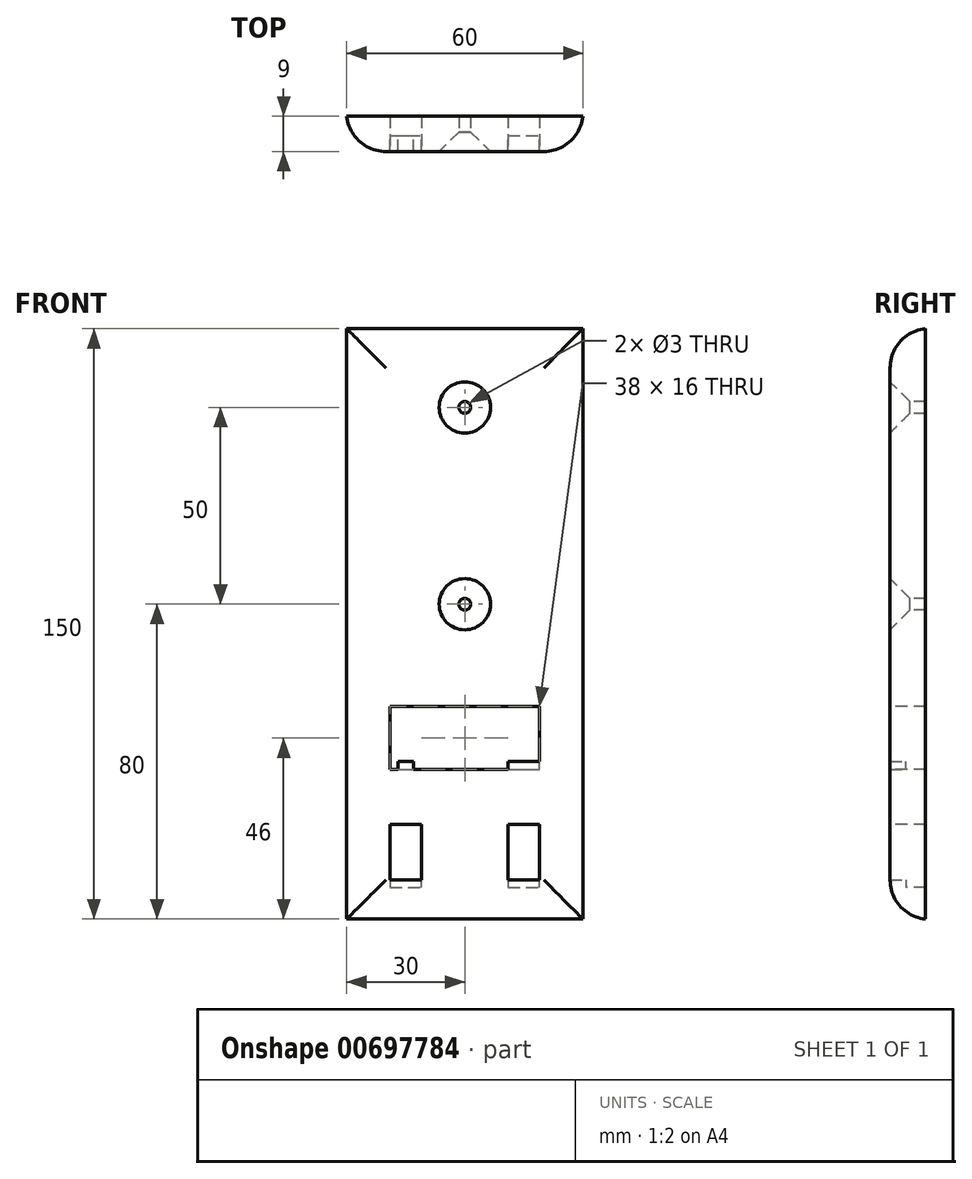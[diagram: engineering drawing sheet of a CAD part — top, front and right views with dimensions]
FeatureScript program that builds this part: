
annotation { "Feature Type Name" : "Feature", "Feature Type Description" : "" }
export const myFeature = defineFeature(function(context is Context, id is Id, definition is map)
    precondition{}
    {
        {
            var Q0;
            Q0=qCreatedBy(makeId("Front.planeOp"),FACE);
            var sketch = newSketch(context, id + "F0", { "sketchPlane" : qUnion([Q0])});
            skLineSegment(sketch, "E0", {"start": v(0, 0) * mm, "end": v(-30, 0) * mm});
            skLineSegment(sketch, "E1", {"start": v(-30, 0) * mm, "end": v(30, 0) * mm});
            skLineSegment(sketch, "E2", {"start": v(30, 0) * mm, "end": v(30, 80) * mm});
            skLineSegment(sketch, "E3", {"start": v(30, 80) * mm, "end": v(-30, 80) * mm});
            skLineSegment(sketch, "E4", {"start": v(-30, 80) * mm, "end": v(-30, 0) * mm});
            skLineSegment(sketch, "E5", {"start": v(-30, 0) * mm, "end": v(-30, 50) * mm, "construction": true});
            skLineSegment(sketch, "E6", {"start": v(-30, 50) * mm, "end": v(30, 50) * mm, "construction": true});
            skLineSegment(sketch, "E7", {"start": v(30, 50) * mm, "end": v(0, 50) * mm, "construction": true});
            skLineSegment(sketch, "E8", {"start": v(0, 50) * mm, "end": v(0, 20) * mm, "construction": true});
            skLineSegment(sketch, "E9", {"start": v(0, 20) * mm, "end": v(30, 20) * mm, "construction": true});
            skLineSegment(sketch, "E10", {"start": v(30, 20) * mm, "end": v(-30, 20) * mm, "construction": true});
            skPoint(sketch, "E10.endSnap0", {"position": v(15, 20) * mm});
            skLineSegment(sketch, "E11.bottom", {"start": v(15, 50) * mm, "end": v(-15, 50) * mm, "construction": true});
            skLineSegment(sketch, "E11.top", {"start": v(15, 20) * mm, "end": v(-15, 20) * mm, "construction": true});
            skLineSegment(sketch, "E11.left", {"start": v(15, 50) * mm, "end": v(15, 20) * mm, "construction": true});
            skLineSegment(sketch, "E11.right", {"start": v(-15, 50) * mm, "end": v(-15, 20) * mm, "construction": true});
            skPoint(sketch, "E11.middle", {"position": v(0, 35) * mm});
            skLineSegment(sketch, "E12", {"start": v(-15, 50) * mm, "end": v(15, 20) * mm, "construction": true});
            skLineSegment(sketch, "E13", {"start": v(15, 50) * mm, "end": v(-15, 20) * mm, "construction": true});
            skLineSegment(sketch, "E14.bottom", {"start": v(-11, 46) * mm, "end": v(-19, 46) * mm});
            skLineSegment(sketch, "E14.top", {"start": v(-11, 54) * mm, "end": v(-19, 54) * mm});
            skLineSegment(sketch, "E14.left", {"start": v(-11, 46) * mm, "end": v(-11, 54) * mm});
            skLineSegment(sketch, "E14.right", {"start": v(-19, 46) * mm, "end": v(-19, 54) * mm});
            skPoint(sketch, "E14.middle", {"position": v(-15, 50) * mm});
            skLineSegment(sketch, "E15.bottom", {"start": v(19, 46) * mm, "end": v(11, 46) * mm});
            skLineSegment(sketch, "E15.top", {"start": v(19, 54) * mm, "end": v(11, 54) * mm});
            skLineSegment(sketch, "E15.left", {"start": v(19, 46) * mm, "end": v(19, 54) * mm});
            skLineSegment(sketch, "E15.right", {"start": v(11, 46) * mm, "end": v(11, 54) * mm});
            skPoint(sketch, "E15.middle", {"position": v(15, 50) * mm});
            skLineSegment(sketch, "E16.bottom", {"start": v(-11, 16) * mm, "end": v(-19, 16) * mm});
            skLineSegment(sketch, "E16.top", {"start": v(-11, 24) * mm, "end": v(-19, 24) * mm});
            skLineSegment(sketch, "E16.left", {"start": v(-11, 16) * mm, "end": v(-11, 24) * mm});
            skLineSegment(sketch, "E16.right", {"start": v(-19, 16) * mm, "end": v(-19, 24) * mm});
            skPoint(sketch, "E16.middle", {"position": v(-15, 20) * mm});
            skLineSegment(sketch, "E17.bottom", {"start": v(19, 16) * mm, "end": v(11, 16) * mm});
            skLineSegment(sketch, "E17.top", {"start": v(19, 24) * mm, "end": v(11, 24) * mm});
            skLineSegment(sketch, "E17.left", {"start": v(19, 16) * mm, "end": v(19, 24) * mm});
            skLineSegment(sketch, "E17.right", {"start": v(11, 16) * mm, "end": v(11, 24) * mm});
            skLineSegment(sketch, "E18.bottom", {"start": v(-19, 46) * mm, "end": v(-11, 46) * mm});
            skLineSegment(sketch, "E18.left", {"start": v(-19, 46) * mm, "end": v(-19, 48) * mm});
            skLineSegment(sketch, "E18.right", {"start": v(-11, 46) * mm, "end": v(-11, 48) * mm});
            skLineSegment(sketch, "E19.top", {"start": v(-19, 38) * mm, "end": v(-11, 38) * mm});
            skLineSegment(sketch, "E19.left", {"start": v(-19, 46) * mm, "end": v(-19, 38) * mm});
            skLineSegment(sketch, "E19.right", {"start": v(-11, 46) * mm, "end": v(-11, 38) * mm});
            skLineSegment(sketch, "E20.bottom", {"start": v(11, 46) * mm, "end": v(19, 46) * mm});
            skLineSegment(sketch, "E20.top", {"start": v(11, 38) * mm, "end": v(19, 38) * mm});
            skLineSegment(sketch, "E20.left", {"start": v(11, 46) * mm, "end": v(11, 38) * mm});
            skLineSegment(sketch, "E20.right", {"start": v(19, 46) * mm, "end": v(19, 38) * mm});
            skLineSegment(sketch, "E21.bottom", {"start": v(-19, 16) * mm, "end": v(-11, 16) * mm});
            skLineSegment(sketch, "E21.top", {"start": v(-19, 8) * mm, "end": v(-11, 8) * mm});
            skLineSegment(sketch, "E21.left", {"start": v(-19, 16) * mm, "end": v(-19, 8) * mm});
            skLineSegment(sketch, "E21.right", {"start": v(-11, 16) * mm, "end": v(-11, 8) * mm});
            skLineSegment(sketch, "E22.bottom", {"start": v(11, 16) * mm, "end": v(19, 16) * mm});
            skLineSegment(sketch, "E22.top", {"start": v(11, 8) * mm, "end": v(19, 8) * mm});
            skLineSegment(sketch, "E22.left", {"start": v(11, 16) * mm, "end": v(11, 8) * mm});
            skLineSegment(sketch, "E22.right", {"start": v(19, 16) * mm, "end": v(19, 8) * mm});
            skLineSegment(sketch, "E23.bottom", {"start": v(-19, 46) * mm, "end": v(-17, 46) * mm});
            skLineSegment(sketch, "E23.top", {"start": v(-19, 38) * mm, "end": v(-17, 38) * mm});
            skLineSegment(sketch, "E23.right", {"start": v(-17, 46) * mm, "end": v(-17, 38) * mm});
            skLineSegment(sketch, "E24.bottom", {"start": v(-11, 46) * mm, "end": v(-13, 46) * mm});
            skLineSegment(sketch, "E24.top", {"start": v(-11, 38) * mm, "end": v(-13, 38) * mm});
            skLineSegment(sketch, "E24.right", {"start": v(-13, 46) * mm, "end": v(-13, 38) * mm});
            skLineSegment(sketch, "E25.bottom", {"start": v(11, 46) * mm, "end": v(13, 46) * mm});
            skLineSegment(sketch, "E25.top", {"start": v(11, 38) * mm, "end": v(13, 38) * mm});
            skLineSegment(sketch, "E25.right", {"start": v(13, 46) * mm, "end": v(13, 38) * mm});
            skLineSegment(sketch, "E26.bottom", {"start": v(19, 46) * mm, "end": v(17, 46) * mm});
            skLineSegment(sketch, "E26.top", {"start": v(19, 38) * mm, "end": v(17, 38) * mm});
            skLineSegment(sketch, "E26.right", {"start": v(17, 46) * mm, "end": v(17, 38) * mm});
            skLineSegment(sketch, "E27.bottom", {"start": v(19, 16) * mm, "end": v(17, 16) * mm});
            skLineSegment(sketch, "E27.top", {"start": v(19, 8) * mm, "end": v(17, 8) * mm});
            skLineSegment(sketch, "E28.bottom", {"start": v(-11, 16) * mm, "end": v(-13, 16) * mm});
            skLineSegment(sketch, "E28.top", {"start": v(-11, 8) * mm, "end": v(-13, 8) * mm});
            skLineSegment(sketch, "E28.right", {"start": v(-13, 16) * mm, "end": v(-13, 8) * mm});
            skLineSegment(sketch, "E29.right", {"start": v(17, 16) * mm, "end": v(17, 8) * mm});
            skLineSegment(sketch, "E30.bottom", {"start": v(11, 16) * mm, "end": v(13, 16) * mm});
            skLineSegment(sketch, "E30.top", {"start": v(11, 8) * mm, "end": v(13, 8) * mm});
            skLineSegment(sketch, "E30.right", {"start": v(13, 16) * mm, "end": v(13, 8) * mm});
            skLineSegment(sketch, "E31.bottom", {"start": v(-19, 16) * mm, "end": v(-17, 16) * mm});
            skLineSegment(sketch, "E31.top", {"start": v(-19, 8) * mm, "end": v(-17, 8) * mm});
            skLineSegment(sketch, "E31.right", {"start": v(-17, 16) * mm, "end": v(-17, 8) * mm});
            skLineSegment(sketch, "E32.top", {"start": v(-19, 40) * mm, "end": v(-11, 40) * mm});
            skLineSegment(sketch, "E32.left", {"start": v(-19, 38) * mm, "end": v(-19, 40) * mm});
            skLineSegment(sketch, "E32.right", {"start": v(-11, 38) * mm, "end": v(-11, 40) * mm});
            skLineSegment(sketch, "E33", {"start": v(11, 40) * mm, "end": v(19, 40) * mm});
            skLineSegment(sketch, "E34", {"start": v(-11, 10) * mm, "end": v(-19, 10) * mm});
            skLineSegment(sketch, "E35", {"start": v(11, 10) * mm, "end": v(19, 10) * mm});
            skLineSegment(sketch, "E36.top", {"start": v(-30, 150) * mm, "end": v(30, 150) * mm});
            skLineSegment(sketch, "E36.left", {"start": v(-30, 0) * mm, "end": v(-30, 150) * mm});
            skLineSegment(sketch, "E36.right", {"start": v(30, 0) * mm, "end": v(30, 150) * mm});
            skLineSegment(sketch, "E37", {"start": v(0, 150) * mm, "end": v(0, 80) * mm, "construction": true});
            skLineSegment(sketch, "E38", {"start": v(0, 80) * mm, "end": v(0, 50) * mm, "construction": true});
            skLineSegment(sketch, "E39", {"start": v(0, 150) * mm, "end": v(0, 130) * mm, "construction": true});
            skLineSegment(sketch, "E40", {"start": v(0, 130) * mm, "end": v(0, 80) * mm, "construction": true});
            skCircle(sketch, "E41", {"center": v(0, 130) * mm, "radius": 1.5 * mm});
            skCircle(sketch, "E42", {"center": v(0, 80) * mm, "radius": 1.5 * mm});
            skLineSegment(sketch, "E43", {"start": v(-11, 54) * mm, "end": v(11, 54) * mm});
            skLineSegment(sketch, "E44", {"start": v(11, 40) * mm, "end": v(-11, 40) * mm});
            skLineSegment(sketch, "E45", {"start": v(11, 38) * mm, "end": v(-11, 38) * mm});
            skSolve(sketch);
        }
        {
            var Q0;
            {var subQ3=sQuery(id+"F0.wireOp",EDGE,"E36.top");Q0=makeQuery(id+"F0.imprint","IMPRINT",FACE,{"disambiguationData":[TD([[makeQuery(id+"F0.imprint","IMPRINT",EDGE,{"derivedFrom":subQ3}),-1.0]])]});}
            var Q1;
            Q1=makeQuery(id+"F0.imprint","IMPRINT",FACE,{"disambiguationData":[TD([[makeQuery(id+"F0.imprint","IMPRINT",EDGE,{"derivedFrom":sQuery(id+"F0.wireOp",EDGE,"E14.top")}),-1.0]])]});
            extrude(context, id + "F1", {"entities" : qUnion([Q0, Q1]), "oppositeDirection" : true, "depth" : 5 * mm, "offsetDistance" : 25 * mm});
        }
        {
            var Q0;
            {var subQ0=sQuery(id+"F0.wireOp",EDGE,"E23.bottom");Q0=makeQuery(id+"F0.imprint","IMPRINT",FACE,{"disambiguationData":[TD([[makeQuery(id+"F0.imprint","IMPRINT",EDGE,{"derivedFrom":subQ0}),-1.0]])]});}
            var Q1;
            {var subQ5=sQuery(id+"F0.wireOp",EDGE,"E32.left");Q1=makeQuery(id+"F0.imprint","IMPRINT",FACE,{"disambiguationData":[TD([[makeQuery(id+"F0.imprint","IMPRINT",EDGE,{"derivedFrom":subQ5}),-1.0]])]});}
            var Q2;
            {var subQ0=sQuery(id+"F0.wireOp",EDGE,"E19.top");var subQ1=sQuery(id+"F0.wireOp",EDGE,"E23.right");var subQ2=makeQuery(id+"F0.imprint","INTERSECT",VERTEX,{"derivedFrom":[subQ1,subQ0]});Q2=makeQuery(id+"F0.imprint","IMPRINT",FACE,{"disambiguationData":[TD([[makeQuery(id+"F0.imprint","IMPRINT",EDGE,{"disambiguationData":[TD([[subQ2,1.0]])],"derivedFrom":subQ1}),1.0]])]});}
            var Q3;
            {var subQ5=sQuery(id+"F0.wireOp",EDGE,"E32.right");Q3=makeQuery(id+"F0.imprint","IMPRINT",FACE,{"disambiguationData":[TD([[makeQuery(id+"F0.imprint","IMPRINT",EDGE,{"derivedFrom":subQ5}),1.0]])]});}
            var Q4;
            {var subQ0=sQuery(id+"F0.wireOp",EDGE,"E25.top");Q4=makeQuery(id+"F0.imprint","IMPRINT",FACE,{"disambiguationData":[TD([[makeQuery(id+"F0.imprint","IMPRINT",EDGE,{"derivedFrom":subQ0}),1.0]])]});}
            var Q5;
            {var subQ0=sQuery(id+"F0.wireOp",EDGE,"E20.top");Q5=makeQuery(id+"F0.imprint","IMPRINT",FACE,{"disambiguationData":[TD([[makeQuery(id+"F0.imprint","IMPRINT",EDGE,{"derivedFrom":subQ0}),1.0]])]});}
            var Q6;
            {var subQ0=sQuery(id+"F0.wireOp",EDGE,"E26.top");Q6=makeQuery(id+"F0.imprint","IMPRINT",FACE,{"disambiguationData":[TD([[makeQuery(id+"F0.imprint","IMPRINT",EDGE,{"derivedFrom":subQ0}),-1.0]])]});}
            var Q7;
            {var subQ0=sQuery(id+"F0.wireOp",EDGE,"E26.bottom");Q7=makeQuery(id+"F0.imprint","IMPRINT",FACE,{"disambiguationData":[TD([[makeQuery(id+"F0.imprint","IMPRINT",EDGE,{"derivedFrom":subQ0}),1.0]])]});}
            var Q8;
            {var subQ0=sQuery(id+"F0.wireOp",EDGE,"NN5jano5-v2yu-koeT-qmYi-EJZCYhMvK6H8.bottom");Q8=makeQuery(id+"F0.imprint","IMPRINT",FACE,{"disambiguationData":[TD([[makeQuery(id+"F0.imprint","IMPRINT",EDGE,{"derivedFrom":subQ0}),-1.0]])]});}
            var Q9;
            {var subQ0=sQuery(id+"F0.wireOp",EDGE,"NN5jano5-v2yu-koeT-qmYi-EJZCYhMvK6H8.top");Q9=makeQuery(id+"F0.imprint","IMPRINT",FACE,{"disambiguationData":[TD([[makeQuery(id+"F0.imprint","IMPRINT",EDGE,{"derivedFrom":subQ0}),1.0]])]});}
            var Q10;
            {var subQ0=sQuery(id+"F0.wireOp",EDGE,"EvVcPynJ-Of4R-KM36-nz1v-TSqms22A6YGf.top");Q10=makeQuery(id+"F0.imprint","IMPRINT",FACE,{"disambiguationData":[TD([[makeQuery(id+"F0.imprint","IMPRINT",EDGE,{"derivedFrom":subQ0}),1.0]])]});}
            var Q11;
            {var subQ0=sQuery(id+"F0.wireOp",EDGE,"xoLzNPPj-sGxH-p6tm-CG6E-vPTKjg17kD3K.top");Q11=makeQuery(id+"F0.imprint","IMPRINT",FACE,{"disambiguationData":[TD([[makeQuery(id+"F0.imprint","IMPRINT",EDGE,{"derivedFrom":subQ0}),1.0]])]});}
            var Q12;
            {var subQ0=sQuery(id+"F0.wireOp",EDGE,"xoLzNPPj-sGxH-p6tm-CG6E-vPTKjg17kD3K.bottom");Q12=makeQuery(id+"F0.imprint","IMPRINT",FACE,{"disambiguationData":[TD([[makeQuery(id+"F0.imprint","IMPRINT",EDGE,{"derivedFrom":subQ0}),-1.0]])]});}
            var Q13;
            {var subQ0=sQuery(id+"F0.wireOp",EDGE,"E31.bottom");Q13=makeQuery(id+"F0.imprint","IMPRINT",FACE,{"disambiguationData":[TD([[makeQuery(id+"F0.imprint","IMPRINT",EDGE,{"derivedFrom":subQ0}),-1.0]])]});}
            var Q14;
            {var subQ0=sQuery(id+"F0.wireOp",EDGE,"E31.top");Q14=makeQuery(id+"F0.imprint","IMPRINT",FACE,{"disambiguationData":[TD([[makeQuery(id+"F0.imprint","IMPRINT",EDGE,{"derivedFrom":subQ0}),1.0]])]});}
            var Q15;
            {var subQ0=sQuery(id+"F0.wireOp",EDGE,"E21.top");Q15=makeQuery(id+"F0.imprint","IMPRINT",FACE,{"disambiguationData":[TD([[makeQuery(id+"F0.imprint","IMPRINT",EDGE,{"derivedFrom":subQ0}),1.0]])]});}
            var Q16;
            {var subQ0=sQuery(id+"F0.wireOp",EDGE,"E28.top");Q16=makeQuery(id+"F0.imprint","IMPRINT",FACE,{"disambiguationData":[TD([[makeQuery(id+"F0.imprint","IMPRINT",EDGE,{"derivedFrom":subQ0}),-1.0]])]});}
            var Q17;
            {var subQ0=sQuery(id+"F0.wireOp",EDGE,"E28.bottom");Q17=makeQuery(id+"F0.imprint","IMPRINT",FACE,{"disambiguationData":[TD([[makeQuery(id+"F0.imprint","IMPRINT",EDGE,{"derivedFrom":subQ0}),1.0]])]});}
            var Q18;
            {var subQ0=sQuery(id+"F0.wireOp",EDGE,"E30.bottom");Q18=makeQuery(id+"F0.imprint","IMPRINT",FACE,{"disambiguationData":[TD([[makeQuery(id+"F0.imprint","IMPRINT",EDGE,{"derivedFrom":subQ0}),-1.0]])]});}
            var Q19;
            {var subQ0=sQuery(id+"F0.wireOp",EDGE,"E30.top");Q19=makeQuery(id+"F0.imprint","IMPRINT",FACE,{"disambiguationData":[TD([[makeQuery(id+"F0.imprint","IMPRINT",EDGE,{"derivedFrom":subQ0}),1.0]])]});}
            var Q20;
            {var subQ0=sQuery(id+"F0.wireOp",EDGE,"E27.bottom");Q20=makeQuery(id+"F0.imprint","IMPRINT",FACE,{"disambiguationData":[TD([[makeQuery(id+"F0.imprint","IMPRINT",EDGE,{"derivedFrom":subQ0}),1.0]])]});}
            var Q21;
            {var subQ0=sQuery(id+"F0.wireOp",EDGE,"E22.top");Q21=makeQuery(id+"F0.imprint","IMPRINT",FACE,{"disambiguationData":[TD([[makeQuery(id+"F0.imprint","IMPRINT",EDGE,{"derivedFrom":subQ0}),1.0]])]});}
            var Q22;
            {var subQ0=sQuery(id+"F0.wireOp",EDGE,"E27.top");Q22=makeQuery(id+"F0.imprint","IMPRINT",FACE,{"disambiguationData":[TD([[makeQuery(id+"F0.imprint","IMPRINT",EDGE,{"derivedFrom":subQ0}),-1.0]])]});}
            var Q23;
            Q23=makeQuery(id+"F0.imprint","IMPRINT",FACE,{"disambiguationData":[TD([[makeQuery(id+"F0.imprint","IMPRINT",EDGE,{"derivedFrom":sQuery(id+"F0.wireOp",EDGE,"E14.top")}),-1.0]])]});
            var Q24;
            {var subQ3=sQuery(id+"F0.wireOp",EDGE,"E36.top");Q24=makeQuery(id+"F0.imprint","IMPRINT",FACE,{"disambiguationData":[TD([[makeQuery(id+"F0.imprint","IMPRINT",EDGE,{"derivedFrom":subQ3}),-1.0]])]});}
            var Q25;
            Q25=makeQuery(id+"F0.imprint","IMPRINT",FACE,{"disambiguationData":[TD([[makeQuery(id+"F0.imprint","IMPRINT",EDGE,{"derivedFrom":sQuery(id+"F0.wireOp",EDGE,"E32.right")}),-1.0]])]});
            extrude(context, id + "F2", {"entities" : qUnion([Q0, Q1, Q2, Q3, Q4, Q5, Q6, Q7, Q8, Q9, Q10, Q11, Q12, Q13, Q14, Q15, Q16, Q17, Q18, Q19, Q20, Q21, Q22, Q23, Q24, Q25]), "operationType" : NewBodyOperationType.ADD, "depth" : 4 * mm, "offsetDistance" : 25 * mm});
        }
        {
            var Q0;
            Q0=makeQuery(id+"F2.opExtrude","CAP_EDGE",EDGE,{"disambiguationData":[OSD([sQuery(id+"F0.wireOp",EDGE,"E41")])],"isStart":false});
            var Q1;
            Q1=makeQuery(id+"F2.opExtrude","CAP_EDGE",EDGE,{"disambiguationData":[OSD([sQuery(id+"F0.wireOp",EDGE,"E42")])],"isStart":false});
            chamfer(context, id + "F3", {"entities" : qUnion([Q0, Q1]), "width" : 5 * mm, "tangentPropagation" : true});
        }
        {
            var Q0;
            Q0=makeQuery(id+"F2.opExtrude","CAP_EDGE",EDGE,{"disambiguationData":[OSD([sQuery(id+"F0.wireOp",EDGE,"E1")])],"isStart":false});
            var Q1;
            Q1=makeQuery(id+"F2.opExtrude","CAP_EDGE",EDGE,{"disambiguationData":[OSD([sQuery(id+"F0.wireOp",EDGE,"E36.left")])],"isStart":false});
            var Q2;
            Q2=makeQuery(id+"F2.opExtrude","CAP_EDGE",EDGE,{"disambiguationData":[OSD([sQuery(id+"F0.wireOp",EDGE,"E36.right")])],"isStart":false});
            var Q3;
            Q3=makeQuery(id+"F2.opExtrude","CAP_EDGE",EDGE,{"disambiguationData":[OSD([sQuery(id+"F0.wireOp",EDGE,"E36.top")])],"isStart":false});
            fillet(context, id + "F4", {"entities" : qUnion([Q0, Q1, Q2, Q3]), "radius" : 10 * mm, "tangentPropagation" : true, "allowEdgeOverflow" : false});
        }
    });
